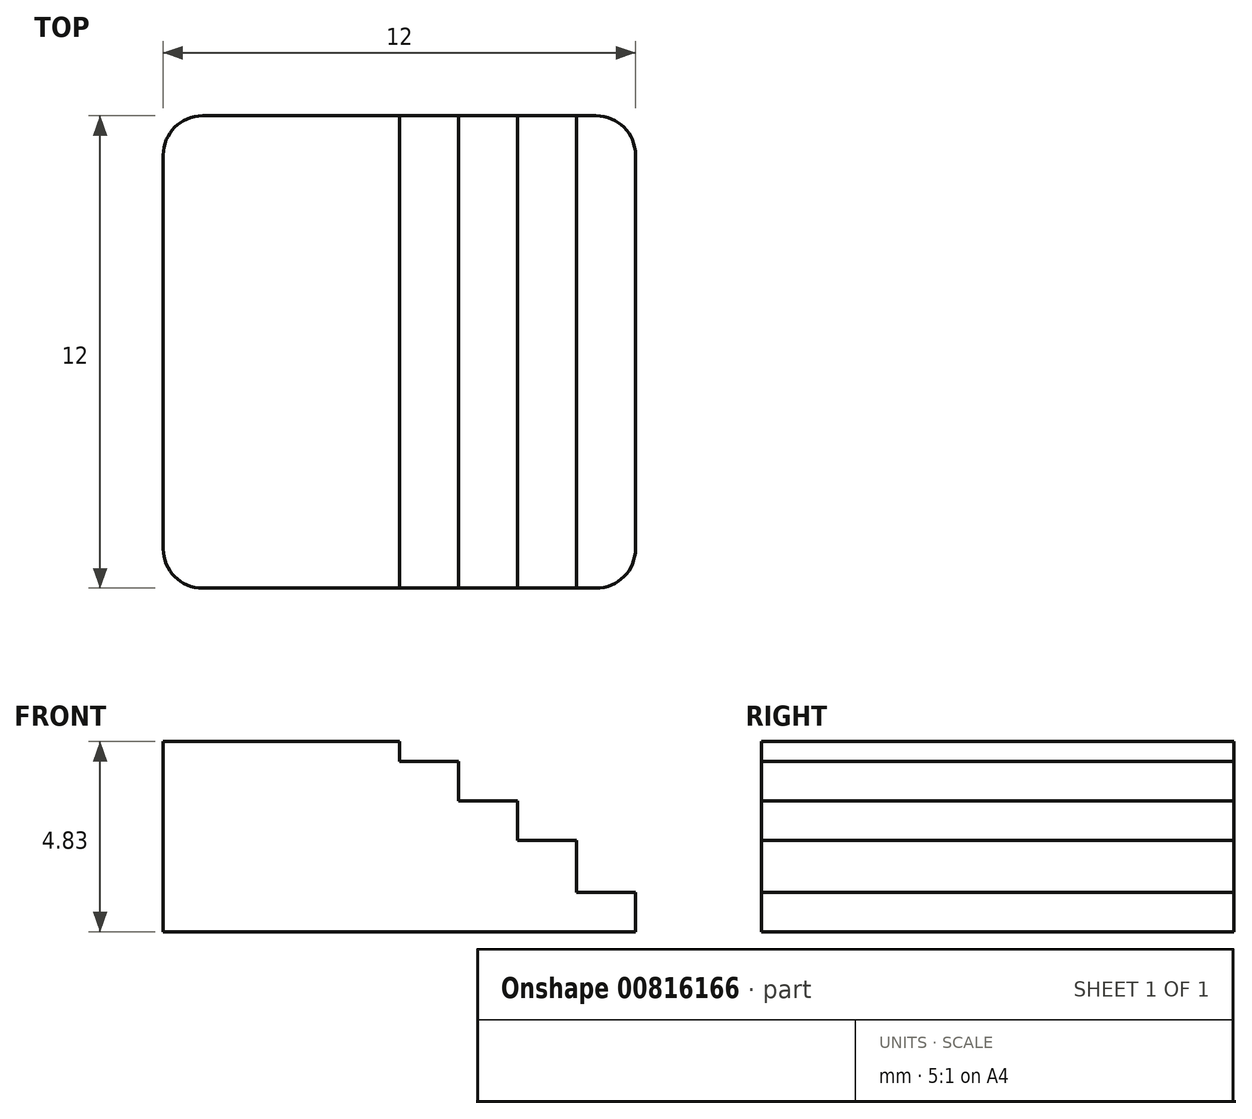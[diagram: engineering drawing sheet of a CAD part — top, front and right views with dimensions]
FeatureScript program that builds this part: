
annotation { "Feature Type Name" : "Feature", "Feature Type Description" : "" }
export const myFeature = defineFeature(function(context is Context, id is Id, definition is map)
    precondition{}
    {
        {
            var Q0;
            Q0=qCreatedBy(makeId("Top.planeOp"),FACE);
            var sketch = newSketch(context, id + "F0", { "sketchPlane" : qUnion([Q0])});
            skLineSegment(sketch, "E0.bottom", {"start": v(6, -6) * mm, "end": v(-6, -6) * mm});
            skLineSegment(sketch, "E0.top", {"start": v(6, 6) * mm, "end": v(-6, 6) * mm});
            skLineSegment(sketch, "E0.left", {"start": v(6, -6) * mm, "end": v(6, 6) * mm});
            skLineSegment(sketch, "E0.right", {"start": v(-6, -6) * mm, "end": v(-6, 6) * mm});
            skPoint(sketch, "E0.middle", {"position": v(0, 0) * mm});
            skSolve(sketch);
        }
        {
            var Q0;
            Q0=makeQuery(id+"F0.imprint","IMPRINT",FACE,{"disambiguationData":[TD([[makeQuery(id+"F0.imprint","IMPRINT",EDGE,{"derivedFrom":sQuery(id+"F0.wireOp",EDGE,"E0.bottom")}),-1.0]])]});
            extrude(context, id + "F1", {"entities" : qUnion([Q0]), "depth" : 4.83 * mm, "offsetDistance" : 25 * mm});
        }
        {
            var Q0;
            Q0=makeQuery(id+"F1.opExtrude","SWEPT_FACE",FACE,{"disambiguationData":[OSD([sQuery(id+"F0.wireOp",EDGE,"E0.bottom")])]});
            var sketch = newSketch(context, id + "F2", { "sketchPlane" : qUnion([Q0])});
            skLineSegment(sketch, "E1.bottom", {"start": v(4.5, 1) * mm, "end": v(7.09, 1) * mm});
            skLineSegment(sketch, "E1.left", {"start": v(4.5, 1) * mm, "end": v(4.5, 2.32) * mm});
            skLineSegment(sketch, "E1.right", {"start": v(7.09, 1) * mm, "end": v(7.09, 5.32) * mm});
            skLineSegment(sketch, "E2.bottom", {"start": v(4.5, 2.32) * mm, "end": v(3, 2.32) * mm});
            skLineSegment(sketch, "E2.right", {"start": v(3, 2.32) * mm, "end": v(3, 3.32) * mm});
            skLineSegment(sketch, "E3.bottom", {"start": v(3, 3.32) * mm, "end": v(1.5, 3.32) * mm});
            skLineSegment(sketch, "E3.right", {"start": v(1.5, 3.32) * mm, "end": v(1.5, 4.32) * mm});
            skLineSegment(sketch, "E4.bottom", {"start": v(1.5, 4.32) * mm, "end": v(0, 4.32) * mm});
            skLineSegment(sketch, "E4.top", {"start": v(1.5, 5.32) * mm, "end": v(0, 5.32) * mm});
            skLineSegment(sketch, "E4.right", {"start": v(0, 4.32) * mm, "end": v(0, 5.32) * mm});
            skLineSegment(sketch, "E5", {"start": v(1.5, 5.32) * mm, "end": v(7.09, 5.32) * mm});
            skSolve(sketch);
        }
        {
            var Q0;
            {var subQ0=sQuery(id+"F2.wireOp",EDGE,"E1.left");Q0=makeQuery(id+"F2.imprint","IMPRINT",FACE,{"disambiguationData":[TD([[makeQuery(id+"F2.imprint","IMPRINT",EDGE,{"derivedFrom":subQ0}),-1.0]])]});}
            extrude(context, id + "F3", {"entities" : qUnion([Q0]), "operationType" : NewBodyOperationType.REMOVE, "oppositeDirection" : true, "depth" : 25 * mm, "offsetDistance" : 25 * mm});
        }
        {
            var Q0;
            Q0=makeQuery(id+"F1.opExtrude","SWEPT_EDGE",EDGE,{"disambiguationData":[OSD([sQuery(id+"F0.wireOp",EDGE,"E0.bottom"),sQuery(id+"F0.wireOp",EDGE,"E0.right")])]});
            var Q1;
            Q1=makeQuery(id+"F1.opExtrude","SWEPT_EDGE",EDGE,{"disambiguationData":[OSD([sQuery(id+"F0.wireOp",EDGE,"E0.top"),sQuery(id+"F0.wireOp",EDGE,"E0.right")])]});
            var Q2;
            Q2=makeQuery(id+"F1.opExtrude","SWEPT_EDGE",EDGE,{"disambiguationData":[OSD([sQuery(id+"F0.wireOp",EDGE,"E0.bottom"),sQuery(id+"F0.wireOp",EDGE,"E0.left")])]});
            var Q3;
            Q3=makeQuery(id+"F1.opExtrude","SWEPT_EDGE",EDGE,{"disambiguationData":[OSD([sQuery(id+"F0.wireOp",EDGE,"E0.top"),sQuery(id+"F0.wireOp",EDGE,"E0.left")])]});
            fillet(context, id + "F4", {"entities" : qUnion([Q0, Q1, Q2, Q3]), "radius" : 1 * mm, "tangentPropagation" : true, "allowEdgeOverflow" : false});
        }
    });
